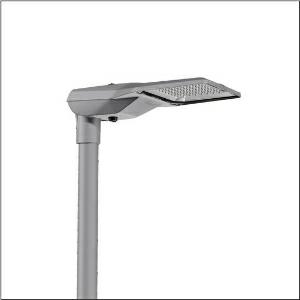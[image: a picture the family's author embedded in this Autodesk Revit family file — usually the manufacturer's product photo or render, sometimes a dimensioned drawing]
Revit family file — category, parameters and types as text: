
# Revit family: streetlight_sl_21_midi___st0_5a_5xe3b33t08nb_f8ff
name_source: partatom
category: Lighting Fixtures
units: mm (PartAtom-declared; Revit-internal decimal feet)

## family parameters
Cut with Voids When Loaded = No
Host = Face
Light Source = No
Part Type = Normal
Room Calculation Point = No
Round Connector Dimension = Use Diameter
Shared = No

## types (1)
- --- (1 x LED, 22700 lm, 151.2 W, 3000K)
    Apparent Load = 151 VA
    CIE Flux Codes = 43 76 97 100 100
    Color Rendering = 70
    Color Temperature = 3000K
    Default Elevation = 1800 mm
    Description = Streetlight SL 21 midi, mast luminaire, primary light control with lens, of PMMA, primary optical cover: cover, of toughened safety glass, transparent, light distribution: ST0.5a, light emission: direct distribution, primary light characteristic: asymmetric, installation type: side-entry, post-top, LED, High Power LED, rated luminous flux: 22.700lm, luminous efficacy: 150lm/W, light colour: 730, colour temperature: 3000K, control gear: D4i, control: overheat protection, constant luminous flux control, time-dependent luminous flux control, flexible luminous flux parameterisation, pre-setting: logarithmic dimming characteristic, mains connection: 230..240V, AC, 50/60Hz, start of lifetime: 151W, end of service life: 157W, reduction: 70W, luminaire housing, of diecast aluminium, powder-coated, SITECO metallic grey (DB 702S), corrosivity category C5 high according to DIN EN ISO 12944, please order mast flange separately, inclination adjustable: 0°, 5°, 10°, 15°, sealing non-destructively replaceable, multi-level sealing system, length: 644mm, width: 335mm, height: 110mm, mast flange for spigot size: 42mm (side-entry): 5XC10008XM4, 60/48mm (side-entry/post-top): 5XC10108XM2, 76/60mm (side-entry/post-top): 5XC10108XM1, mounting height: 4..8m, Smart Interface below and above, protection rating (complete): IP66, insulation class (complete): insulation class II (safety insulation), certification: CE, ENEC, ENEC+, VDE, impact resistance: IK10, permissible operating ambient temperature for outdoor applications: -40..+50°C, standard-compliant lighting for roads and squares, packaging unit: 1 piece

Light Distribution: ST0.5a
    Height = 111 mm
    Lamp = 1 x LED
    Lamp Light Flux = 22700 lm
    Lamp Power = 151.2 W
    Lamp count = 1
    Length = 644 mm
    Luminous efficacy = 150 lm/W
    Manufacturer = Siteco
    ModVariant = No
    Model = 5XE3B33T08NB
    Number of Poles = 1
    OnlyDefault = Yes
    Power Factor = 1
    Product Name = Streetlight SL 21 midi | ST0.5a
    Product group = mast luminaire | pylon top
    ProductGroupID = 6100
    Protection Class = Protection class II
    Protection Degree = IP 66
    RLX_Detail_Level = 1
    RLX_Emergency_Light_Flux = 0 lm
    RLX_Emergency_Type = 0
    RLX_Emergency_Type_DB = No
    RlxData = <blob elided: 38321 chars, md5=e861c5be>
    Socket = socket
    Standby Power = 0 W
    System Light Flux = 22700 lm
    System Power = 151 W
    Type Comments = factory setting: luminous flux: 100 % | dim-lin: 254 | 802 mA
    Type Image = l_1004304.jpg
    URL = http://relux.com
    VarID = @adj_170829
    Voltage = 0 V
    Weight = 0.00 kg
    Width = 336 mm

## geometry (parser evidence)
native form markers: Blend x4, Sweep x11
no freeform markers — native parametric forms only
